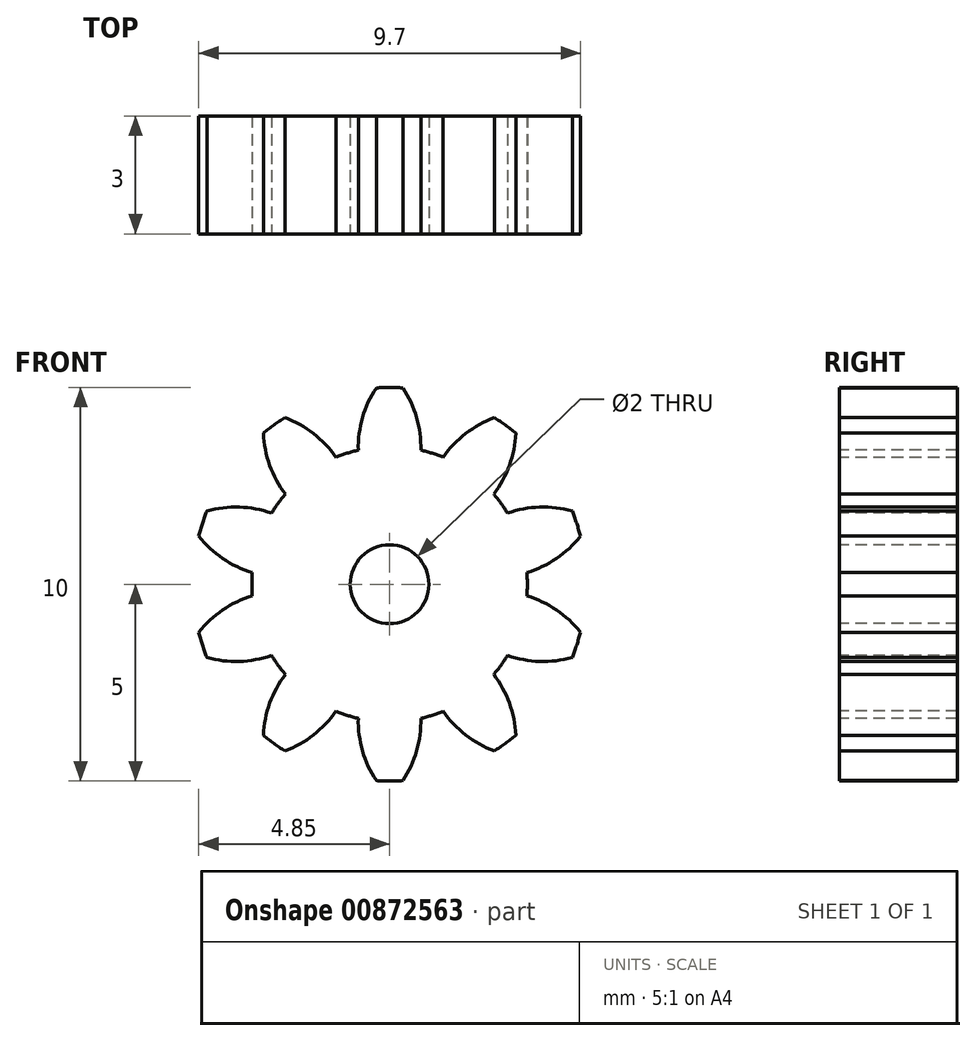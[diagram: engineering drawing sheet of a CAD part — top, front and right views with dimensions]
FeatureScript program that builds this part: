
annotation { "Feature Type Name" : "Feature", "Feature Type Description" : "" }
export const myFeature = defineFeature(function(context is Context, id is Id, definition is map)
    precondition{}
    {
        {
            var Q0;
            Q0=qCreatedBy(makeId("Front.planeOp"),FACE);
            var sketch = newSketch(context, id + "F0", { "sketchPlane" : qUnion([Q0])});
            skCircle(sketch, "E0", {"center": v(0, 0) * mm, "radius": 3.5 * mm});
            skArc(sketch, "E1", {"start": v(0.34, 4.99) * mm, "mid": v(0, 5) * mm, "end": v(-0.34, 4.99) * mm});
            skArc(sketch, "E2", {"start": v(-0.34, 4.99) * mm, "mid": v(-0.69, 4.23) * mm, "end": v(-0.8, 3.4) * mm});
            skArc(sketch, "E3.MirrorCS", {"start": v(0.34, 4.99) * mm, "mid": v(0.69, 4.23) * mm, "end": v(0.8, 3.4) * mm});
            skArc(sketch, "E4.1.0", {"start": v(-2.66, 4.23) * mm, "mid": v(-1.93, 3.83) * mm, "end": v(-1.36, 3.22) * mm});
            skArc(sketch, "E4.1.1", {"start": v(-2.66, 4.23) * mm, "mid": v(-2.94, 4.05) * mm, "end": v(-3.2, 3.84) * mm});
            skArc(sketch, "E4.1.2", {"start": v(-3.2, 3.84) * mm, "mid": v(-3.04, 3.02) * mm, "end": v(-2.65, 2.3) * mm});
            skArc(sketch, "E4.2.0", {"start": v(-4.64, 1.86) * mm, "mid": v(-3.81, 1.96) * mm, "end": v(-3, 1.8) * mm});
            skArc(sketch, "E4.2.1", {"start": v(-4.64, 1.86) * mm, "mid": v(-4.76, 1.55) * mm, "end": v(-4.85, 1.22) * mm});
            skArc(sketch, "E4.2.2", {"start": v(-4.85, 1.22) * mm, "mid": v(-4.24, 0.65) * mm, "end": v(-3.49, 0.3) * mm});
            skArc(sketch, "E4.3.0", {"start": v(-4.85, -1.22) * mm, "mid": v(-4.24, -0.65) * mm, "end": v(-3.49, -0.3) * mm});
            skArc(sketch, "E4.3.1", {"start": v(-4.85, -1.22) * mm, "mid": v(-4.76, -1.55) * mm, "end": v(-4.64, -1.86) * mm});
            skArc(sketch, "E4.3.2", {"start": v(-4.64, -1.86) * mm, "mid": v(-3.81, -1.96) * mm, "end": v(-3, -1.8) * mm});
            skArc(sketch, "E4.4.0", {"start": v(-3.2, -3.84) * mm, "mid": v(-3.04, -3.02) * mm, "end": v(-2.65, -2.3) * mm});
            skArc(sketch, "E4.4.1", {"start": v(-3.2, -3.84) * mm, "mid": v(-2.94, -4.05) * mm, "end": v(-2.66, -4.23) * mm});
            skArc(sketch, "E4.4.2", {"start": v(-2.66, -4.23) * mm, "mid": v(-1.93, -3.83) * mm, "end": v(-1.36, -3.22) * mm});
            skArc(sketch, "E4.5.0", {"start": v(-0.34, -4.99) * mm, "mid": v(-0.69, -4.23) * mm, "end": v(-0.8, -3.4) * mm});
            skArc(sketch, "E4.5.1", {"start": v(-0.34, -4.99) * mm, "mid": v(0, -5) * mm, "end": v(0.34, -4.99) * mm});
            skArc(sketch, "E4.5.2", {"start": v(0.34, -4.99) * mm, "mid": v(0.69, -4.23) * mm, "end": v(0.8, -3.4) * mm});
            skArc(sketch, "E4.6.0", {"start": v(2.66, -4.23) * mm, "mid": v(1.93, -3.83) * mm, "end": v(1.36, -3.22) * mm});
            skArc(sketch, "E4.6.1", {"start": v(2.66, -4.23) * mm, "mid": v(2.94, -4.05) * mm, "end": v(3.2, -3.84) * mm});
            skArc(sketch, "E4.6.2", {"start": v(3.2, -3.84) * mm, "mid": v(3.04, -3.02) * mm, "end": v(2.65, -2.3) * mm});
            skArc(sketch, "E4.7.0", {"start": v(4.64, -1.86) * mm, "mid": v(3.81, -1.96) * mm, "end": v(3, -1.8) * mm});
            skArc(sketch, "E4.7.1", {"start": v(4.64, -1.86) * mm, "mid": v(4.76, -1.55) * mm, "end": v(4.85, -1.22) * mm});
            skArc(sketch, "E4.7.2", {"start": v(4.85, -1.22) * mm, "mid": v(4.24, -0.65) * mm, "end": v(3.49, -0.3) * mm});
            skArc(sketch, "E4.8.0", {"start": v(4.85, 1.22) * mm, "mid": v(4.24, 0.65) * mm, "end": v(3.49, 0.3) * mm});
            skArc(sketch, "E4.8.1", {"start": v(4.85, 1.22) * mm, "mid": v(4.76, 1.55) * mm, "end": v(4.64, 1.86) * mm});
            skArc(sketch, "E4.8.2", {"start": v(4.64, 1.86) * mm, "mid": v(3.81, 1.96) * mm, "end": v(3, 1.8) * mm});
            skArc(sketch, "E5.1.9.0", {"start": v(3.2, 3.84) * mm, "mid": v(3.04, 3.02) * mm, "end": v(2.65, 2.3) * mm});
            skArc(sketch, "E5.4.9.0", {"start": v(3.2, 3.84) * mm, "mid": v(2.94, 4.05) * mm, "end": v(2.66, 4.23) * mm});
            skArc(sketch, "E5.8.9.0", {"start": v(2.66, 4.23) * mm, "mid": v(1.93, 3.83) * mm, "end": v(1.36, 3.22) * mm});
            skSolve(sketch);
        }
        {
            var Q0;
            Q0 = qSketchRegion(id + "F0", true);
            extrude(context, id + "F1", {"entities" : qUnion([Q0]), "oppositeDirection" : true, "depth" : 3 * mm, "offsetDistance" : 25 * mm});
        }
        {
            var Q0;
            Q0=makeQuery(id+"F1.opExtrude","CAP_FACE",FACE,{"disambiguationData":[OSD([sQuery(id+"F0.wireOp",EDGE,"E0"),sQuery(id+"F0.wireOp",EDGE,"E1"),sQuery(id+"F0.wireOp",EDGE,"E2"),sQuery(id+"F0.wireOp",EDGE,"E3.MirrorCS"),sQuery(id+"F0.wireOp",EDGE,"E4.1.0"),sQuery(id+"F0.wireOp",EDGE,"E4.1.1"),sQuery(id+"F0.wireOp",EDGE,"E4.1.2"),sQuery(id+"F0.wireOp",EDGE,"E4.2.0"),sQuery(id+"F0.wireOp",EDGE,"E4.2.1"),sQuery(id+"F0.wireOp",EDGE,"E4.2.2"),sQuery(id+"F0.wireOp",EDGE,"E4.3.0"),sQuery(id+"F0.wireOp",EDGE,"E4.3.1"),sQuery(id+"F0.wireOp",EDGE,"E4.3.2"),sQuery(id+"F0.wireOp",EDGE,"E4.4.0"),sQuery(id+"F0.wireOp",EDGE,"E4.4.1"),sQuery(id+"F0.wireOp",EDGE,"E4.4.2"),sQuery(id+"F0.wireOp",EDGE,"E4.5.0"),sQuery(id+"F0.wireOp",EDGE,"E4.5.1"),sQuery(id+"F0.wireOp",EDGE,"E4.5.2"),sQuery(id+"F0.wireOp",EDGE,"E4.6.0"),sQuery(id+"F0.wireOp",EDGE,"E4.6.1"),sQuery(id+"F0.wireOp",EDGE,"E4.6.2"),sQuery(id+"F0.wireOp",EDGE,"E4.7.0"),sQuery(id+"F0.wireOp",EDGE,"E4.7.1"),sQuery(id+"F0.wireOp",EDGE,"E4.7.2"),sQuery(id+"F0.wireOp",EDGE,"E4.8.0"),sQuery(id+"F0.wireOp",EDGE,"E4.8.1"),sQuery(id+"F0.wireOp",EDGE,"E4.8.2")])],"isStart":true});
            var sketch = newSketch(context, id + "F2", { "sketchPlane" : qUnion([Q0])});
            skCircle(sketch, "E6", {"center": v(0, 0) * mm, "radius": 1 * mm});
            skSolve(sketch);
        }
        {
            var Q0;
            Q0=makeQuery(id+"F2.imprint","IMPRINT",FACE,{"disambiguationData":[TD([[makeQuery(id+"F2.imprint","IMPRINT",EDGE,{"derivedFrom":sQuery(id+"F2.wireOp",EDGE,"E6")}),1.0]])]});
            extrude(context, id + "F3", {"entities" : qUnion([Q0]), "operationType" : NewBodyOperationType.REMOVE, "endBound" : BoundingType.THROUGH_ALL, "oppositeDirection" : true, "depth" : 25 * mm, "offsetDistance" : 25 * mm});
        }
    });
